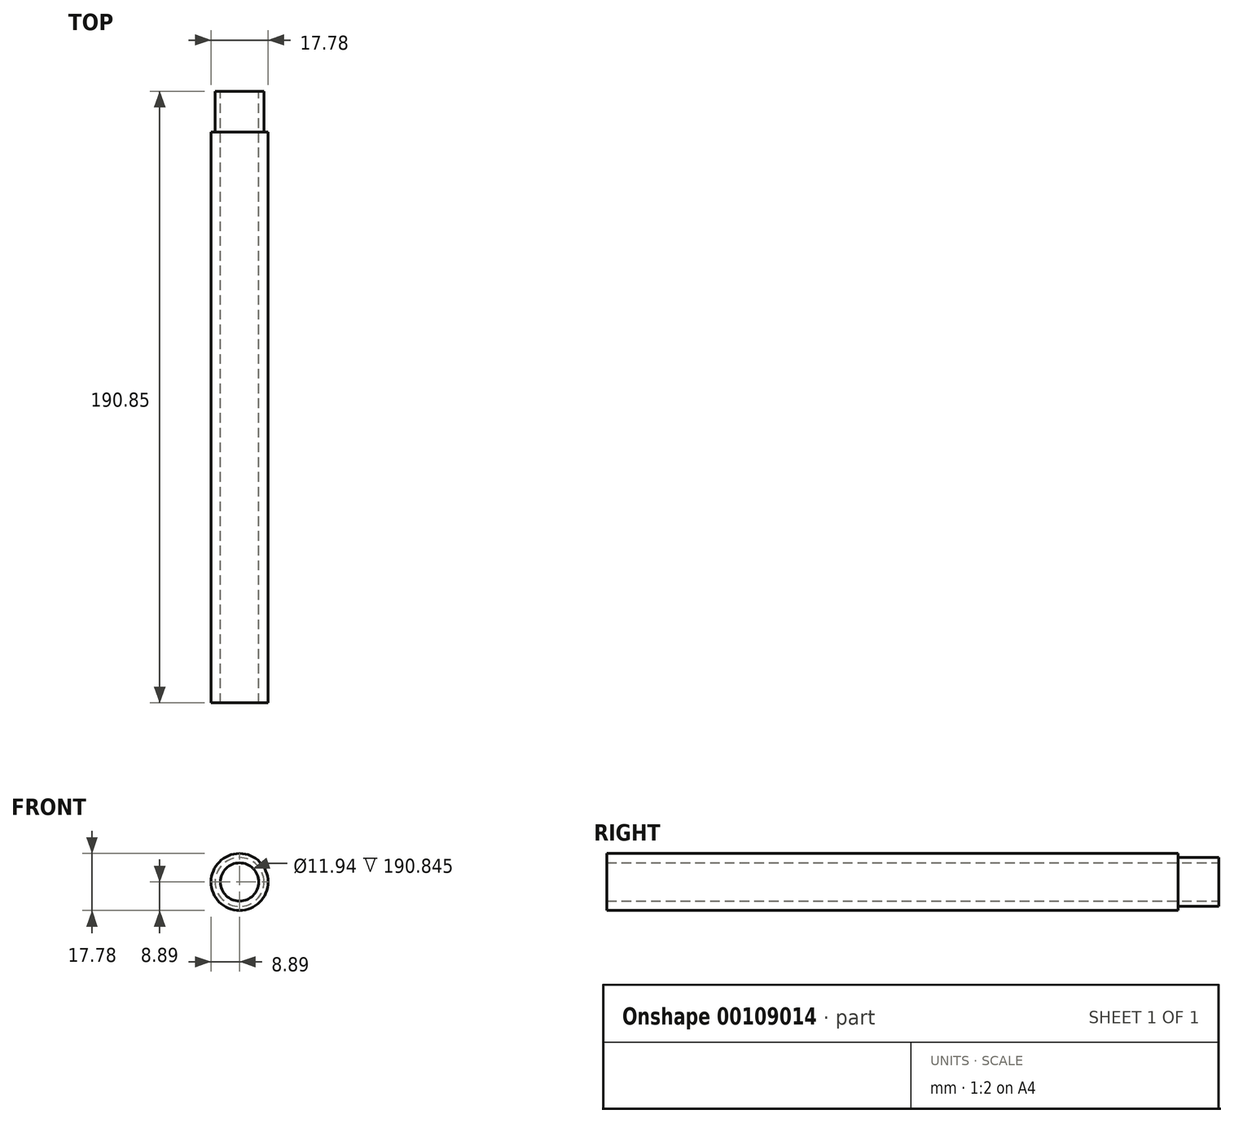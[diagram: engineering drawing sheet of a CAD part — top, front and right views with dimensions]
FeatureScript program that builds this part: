
annotation { "Feature Type Name" : "Feature", "Feature Type Description" : "" }
export const myFeature = defineFeature(function(context is Context, id is Id, definition is map)
    precondition{}
    {
        {
            var Q0;
            Q0=qCreatedBy(makeId("Front.planeOp"),FACE);
            var sketch = newSketch(context, id + "F0", { "sketchPlane" : qUnion([Q0])});
            skCircle(sketch, "E0", {"center": v(0, 0) * mm, "radius": 8.9 * mm});
            skCircle(sketch, "E1", {"center": v(0, 0) * mm, "radius": 5.97 * mm});
            skSolve(sketch);
        }
        {
            var Q0;
            Q0=makeQuery(id+"F0.imprint","IMPRINT",FACE,{"disambiguationData":[TD([[makeQuery(id+"F0.imprint","IMPRINT",EDGE,{"derivedFrom":sQuery(id+"F0.wireOp",EDGE,"E0")}),1.0]])]});
            extrude(context, id + "F1", {"entities" : qUnion([Q0]), "depth" : 178.15 * mm, "hasSecondDirection" : true, "secondDirectionOppositeDirection" : true, "secondDirectionDepth" : 12.7 * mm});
        }
        {
            var Q0;
            Q0=makeQuery(id+"F1.opExtrude","CAP_FACE",FACE,{"disambiguationData":[OSD([sQuery(id+"F0.wireOp",EDGE,"E0"),sQuery(id+"F0.wireOp",EDGE,"E1")])],"isStart":true});
            var sketch = newSketch(context, id + "F2", { "sketchPlane" : qUnion([Q0])});
            skCircle(sketch, "E2", {"center": v(0, 0) * mm, "radius": 7.62 * mm});
            skSolve(sketch);
        }
        {
            var Q0;
            Q0=makeQuery(id+"F2.imprint","IMPRINT",FACE,{"disambiguationData":[TD([[makeQuery(id+"F2.imprint","IMPRINT",EDGE,{"derivedFrom":sQuery(id+"F2.wireOp",EDGE,"E2")}),-1.0]])]});
            extrude(context, id + "F3", {"entities" : qUnion([Q0]), "operationType" : NewBodyOperationType.REMOVE, "oppositeDirection" : true, "depth" : 12.7 * mm});
        }
    });
